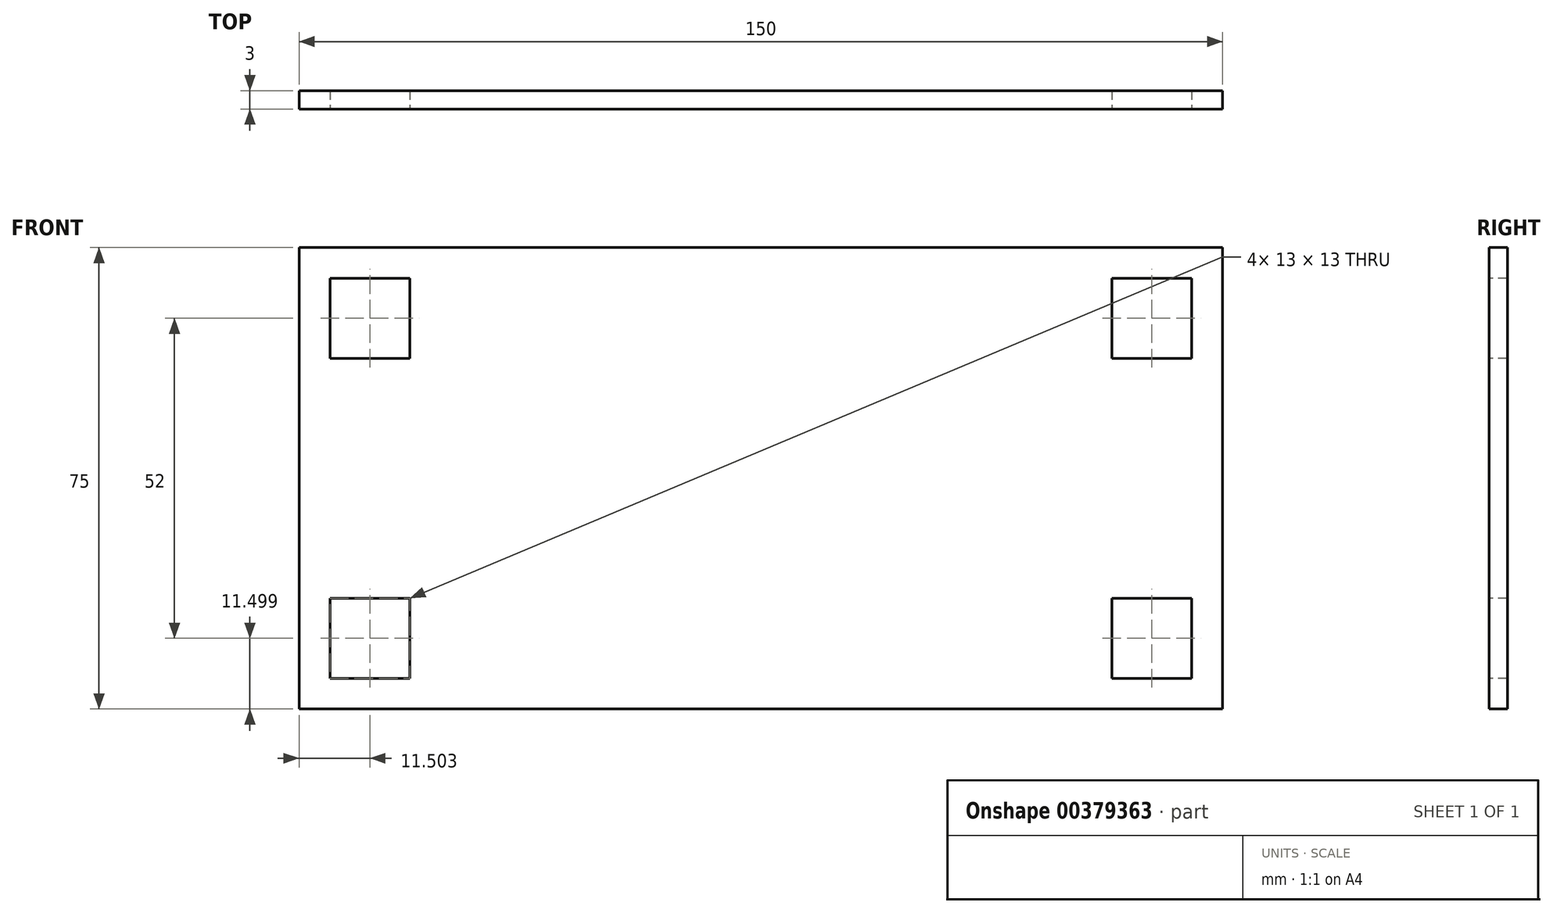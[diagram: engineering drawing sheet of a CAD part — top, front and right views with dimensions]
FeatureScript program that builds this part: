
annotation { "Feature Type Name" : "Feature", "Feature Type Description" : "" }
export const myFeature = defineFeature(function(context is Context, id is Id, definition is map)
    precondition{}
    {
        {
            var Q0;
            Q0=qCreatedBy(makeId("Front.planeOp"),FACE);
            var sketch = newSketch(context, id + "F0", { "sketchPlane" : qUnion([Q0])});
            skLineSegment(sketch, "E0.bottom", {"start": v(-43.02, 83.85) * mm, "end": v(106.98, 83.85) * mm});
            skLineSegment(sketch, "E0.top", {"start": v(-43.02, 8.85) * mm, "end": v(106.98, 8.85) * mm});
            skLineSegment(sketch, "E0.left", {"start": v(-43.02, 83.85) * mm, "end": v(-43.02, 8.85) * mm});
            skLineSegment(sketch, "E0.right", {"start": v(106.98, 83.85) * mm, "end": v(106.98, 8.85) * mm});
            skSolve(sketch);
        }
        {
            var Q0;
            Q0 = qSketchRegion(id + "F0", true);
            extrude(context, id + "F1", {"entities" : qUnion([Q0]), "depth" : 3 * mm, "offsetDistance" : 25 * mm});
        }
        {
            var Q0;
            Q0=makeQuery(id+"F1.opExtrude","CAP_FACE",FACE,{"disambiguationData":[OSD([sQuery(id+"F0.wireOp",EDGE,"E0.bottom"),sQuery(id+"F0.wireOp",EDGE,"E0.top"),sQuery(id+"F0.wireOp",EDGE,"E0.left"),sQuery(id+"F0.wireOp",EDGE,"E0.right")])],"isStart":false});
            var sketch = newSketch(context, id + "F2", { "sketchPlane" : qUnion([Q0])});
            skLineSegment(sketch, "E1.bottom", {"start": v(-38.02, 78.85) * mm, "end": v(-25.02, 78.85) * mm});
            skLineSegment(sketch, "E1.top", {"start": v(-38.02, 65.85) * mm, "end": v(-25.02, 65.85) * mm});
            skLineSegment(sketch, "E1.left", {"start": v(-38.02, 78.85) * mm, "end": v(-38.02, 65.85) * mm});
            skLineSegment(sketch, "E1.right", {"start": v(-25.02, 78.85) * mm, "end": v(-25.02, 65.85) * mm});
            skLineSegment(sketch, "E2.bottom", {"start": v(-38.02, 26.85) * mm, "end": v(-25.02, 26.85) * mm});
            skLineSegment(sketch, "E2.top", {"start": v(-38.02, 13.85) * mm, "end": v(-25.02, 13.85) * mm});
            skLineSegment(sketch, "E2.left", {"start": v(-38.02, 26.85) * mm, "end": v(-38.02, 13.85) * mm});
            skLineSegment(sketch, "E2.right", {"start": v(-25.02, 26.85) * mm, "end": v(-25.02, 13.85) * mm});
            skLineSegment(sketch, "E3.bottom", {"start": v(88.98, 26.85) * mm, "end": v(101.98, 26.85) * mm});
            skLineSegment(sketch, "E3.top", {"start": v(88.98, 13.85) * mm, "end": v(101.98, 13.85) * mm});
            skLineSegment(sketch, "E3.left", {"start": v(88.98, 26.85) * mm, "end": v(88.98, 13.85) * mm});
            skLineSegment(sketch, "E3.right", {"start": v(101.98, 26.85) * mm, "end": v(101.98, 13.85) * mm});
            skLineSegment(sketch, "E4.bottom", {"start": v(101.98, 78.85) * mm, "end": v(88.98, 78.85) * mm});
            skLineSegment(sketch, "E4.top", {"start": v(101.98, 65.85) * mm, "end": v(88.98, 65.85) * mm});
            skLineSegment(sketch, "E4.left", {"start": v(101.98, 78.85) * mm, "end": v(101.98, 65.85) * mm});
            skLineSegment(sketch, "E4.right", {"start": v(88.98, 78.85) * mm, "end": v(88.98, 65.85) * mm});
            skSolve(sketch);
        }
        {
            var Q0;
            Q0 = qSketchRegion(id + "F2", true);
            extrude(context, id + "F3", {"entities" : qUnion([Q0]), "operationType" : NewBodyOperationType.REMOVE, "oppositeDirection" : true, "depth" : 4 * mm, "offsetDistance" : 25 * mm});
        }
    });
